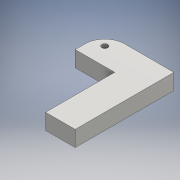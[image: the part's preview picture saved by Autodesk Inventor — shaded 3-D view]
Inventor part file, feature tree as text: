
AUTODESK INVENTOR PART (.ipt)
format: ipt  version: 2016 (Build 200138000, 138)  size: 111,616 bytes
history: native  units: mm
features: sketch x3, extrude x2, fillet x1, hole x1
ambient origin geometry x8: Origin, YZ Plane, XZ Plane, XY Plane, X Axis, Y Axis, Z Axis, Center Point
bodies: Body1 (feature_tree)
feature tree (7):
  extrude  "Extrusion2"  Depth=8.0mm
  extrude  "Extrusion3"  Depth=15.0mm
  fillet  "Fillet1"  Radius=20.0mm
  hole  "Hole1"  [1 undecoded]
  sketch  "Sketch2"  dims[d5=15.0mm d6=8.0mm]
  sketch  "Sketch3"  dims[d7=50.0mm d8=0.0mm d9=15.0mm d10=20.0mm d11=0.0mm]
  sketch  "Sketch5"  dims[d12=10.0mm d13=6.0mm d14=6.0mm d15=3.0mm d16=6.0mm d17=4.0mm d18=2.0mm d19=90.0deg d20=8.0mm d21=20.594885mm]
note: 1 required parameter value undecoded (feature->parameter linkage not recoverable at this tier; creation-order binding heuristic only, values carry confidence <= 0.55)
